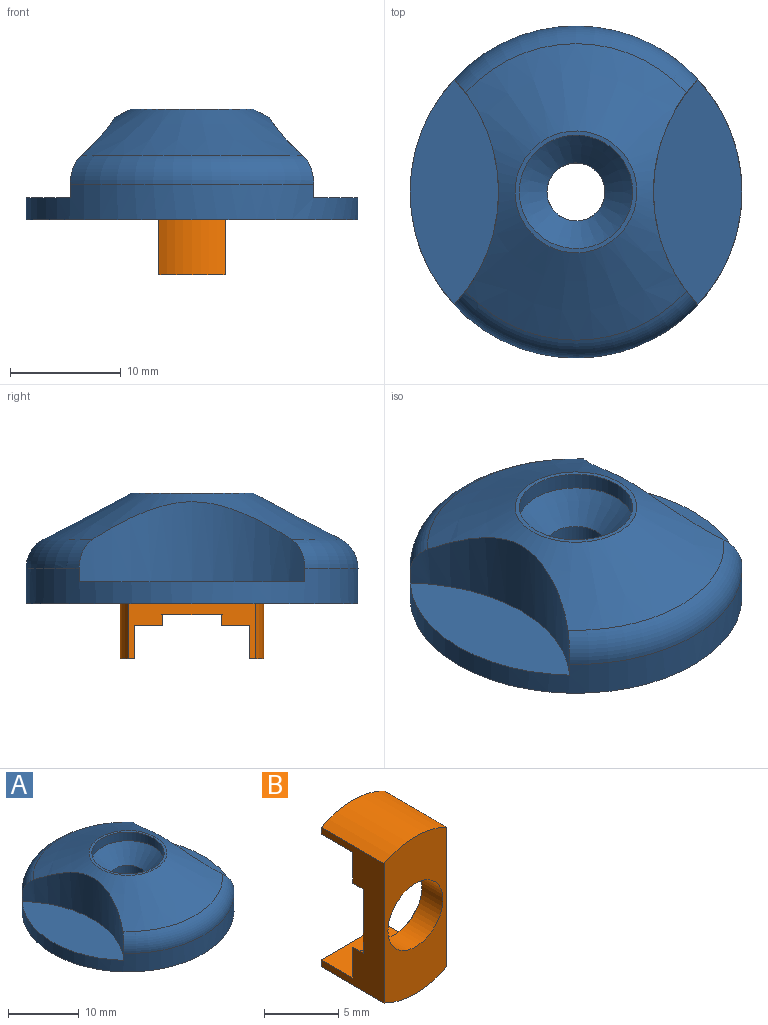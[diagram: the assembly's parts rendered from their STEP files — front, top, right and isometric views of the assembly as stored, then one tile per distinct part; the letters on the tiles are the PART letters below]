
ASSEMBLY  parts=2 mates=1
PART A: 14 faces, bbox 30x32.5x10 mm
  f0: cone r=5.51mm half-angle=62.2deg, axis (0,0,-1), area 352.9mm2, adj f1,f2,f7,f10,f12
  f1: torus R=12.01mm, axis (0,0,-1), area 78.2mm2, adj f0,f3,f10,f12
  f2: torus R=12.01mm, axis (0,0,-1), area 78.2mm2, adj f0,f3,f10,f12
  f3: cylinder r=15mm len=30.01mm, axis (0,0,-1), area 247.3mm2, adj f1,f2,f8,f10,f11,f12,f13
  f4: cylinder r=2.62mm len=5.25mm, axis (0,0,-1), area 82.5mm2, adj f5,f9
  f5: cone r=2.62mm half-angle=45deg, axis (0,0,1), area 86.1mm2, adj f4,f6
  f6: cylinder r=5.12mm len=10.25mm, axis (0,0,-1), area 48.3mm2, adj f5,f7
  f7: plane 11.01x11.01mm, normal (0,0,1), area 12.7mm2, adj f0,f6
  f8: torus R=5mm, axis (0,0,-1), area 633.9mm2, adj f3,f9
  f9: plane 10.01x10.01mm, normal (0,0,-1), area 57mm2, adj f4,f8
  f10: cylinder r=15mm len=20.4mm, axis (0,0,1), area 123.8mm2, adj f0,f1,f2,f3,f11
  f11: plane 20.4x8.01mm, normal (0,0,1), area 112.2mm2, adj f3,f10
  f12: cylinder r=15mm len=20.4mm, axis (0,0,1), area 123.8mm2, adj f0,f1,f2,f3,f13
  f13: plane 20.4x8.01mm, normal (0,0,1), area 112.2mm2, adj f3,f12
PART B: 15 faces, bbox 6x6x13 mm
  f0: plane 6x3mm, normal (0,0,-1), area 18mm2, adj f1,f7,f9,f11
  f1: plane 6x2.55mm, normal (0,1,0), area 9.7mm2, adj f0,f2,f9,f11
  f2: cylinder r=4mm len=6mm, axis (0,-1,0), area 6.8mm2, adj f1,f9,f11,f12
  f3: cylinder r=4mm len=6mm, axis (0,-1,0), area 6.8mm2, adj f4,f9,f11,f12
  f4: plane 6x2.55mm, normal (0,1,0), area 9.7mm2, adj f3,f5,f9,f11
  f5: plane 6x3mm, normal (0,0,1), area 18mm2, adj f4,f6,f9,f11
  f6: plane 6x1.3mm, normal (0,1,0), area 6.4mm2, adj f5,f9,f10,f11
  f7: plane 6x1.3mm, normal (0,1,0), area 6.4mm2, adj f0,f8,f9,f11
  f8: cylinder r=6.5mm len=6mm, axis (0,-1,0), area 37.4mm2, adj f7,f9,f11,f14
  f9: plane 11.53x6mm, normal (1,0,0), area 32.7mm2, adj f0,f1,f2,f3,f4,f5,f6,f7
  f10: cylinder r=6.5mm len=6mm, axis (0,-1,0), area 37.4mm2, adj f6,f9,f11,f14
  f11: plane 11.53x6mm, normal (-1,0,0), area 32.7mm2, adj f0,f1,f2,f3,f4,f5,f6,f7
  f12: plane 8x6mm, normal (0,1,0), area 21.4mm2, adj f2,f3,f9,f11,f13
  f13: cylinder r=2.62mm len=5.25mm, axis (0,-1,0), area 33mm2, adj f12,f14
  f14: plane 13x6mm, normal (0,-1,0), area 53.5mm2, adj f8,f9,f10,f11,f13
PLACE A t=(0,-4.37,-12.18)mm
PLACE B rot(axis=(-1,0,0),90deg) t=(0,-4.37,-12.18)mm
MATE fastened A.f0 <-> B.f13  axis (0,0,-1) through (0,-4.37,-12.18)mm
